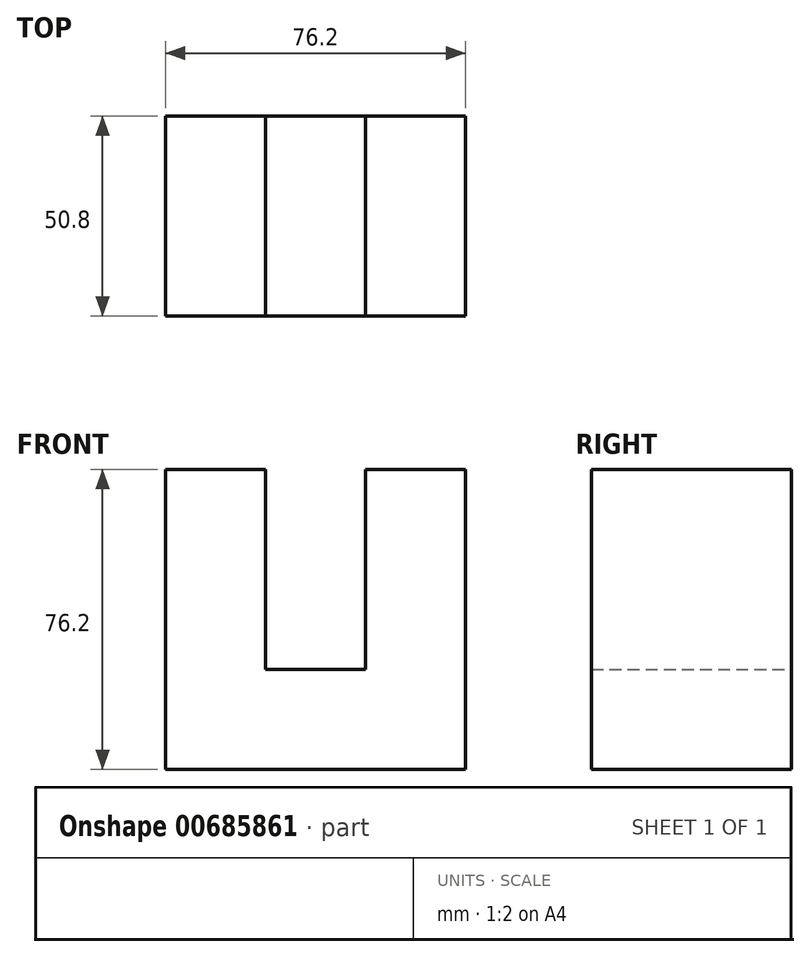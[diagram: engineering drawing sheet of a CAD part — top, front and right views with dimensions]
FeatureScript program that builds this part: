
annotation { "Feature Type Name" : "Feature", "Feature Type Description" : "" }
export const myFeature = defineFeature(function(context is Context, id is Id, definition is map)
    precondition{}
    {
        {
            var Q0;
            Q0=qCreatedBy(makeId("Front.planeOp"),FACE);
            var sketch = newSketch(context, id + "F0", { "sketchPlane" : qUnion([Q0])});
            skLineSegment(sketch, "E0", {"start": v(-27.97, 33.33) * mm, "end": v(-27.97, -42.87) * mm});
            skLineSegment(sketch, "E1", {"start": v(-27.97, 33.33) * mm, "end": v(-2.57, 33.33) * mm});
            skLineSegment(sketch, "E2", {"start": v(-2.57, 33.33) * mm, "end": v(-2.57, -17.47) * mm});
            skLineSegment(sketch, "E3", {"start": v(-2.57, -17.47) * mm, "end": v(22.83, -17.47) * mm});
            skLineSegment(sketch, "E4", {"start": v(22.83, -17.47) * mm, "end": v(22.83, 33.33) * mm});
            skLineSegment(sketch, "E5", {"start": v(22.83, 33.33) * mm, "end": v(48.23, 33.33) * mm});
            skLineSegment(sketch, "E6", {"start": v(48.23, 33.33) * mm, "end": v(48.23, -42.87) * mm});
            skLineSegment(sketch, "E7", {"start": v(48.23, -42.87) * mm, "end": v(-27.97, -42.87) * mm});
            skSolve(sketch);
        }
        {
            var Q0;
            Q0 = qSketchRegion(id + "F0", true);
            extrude(context, id + "F1", {"entities" : qUnion([Q0]), "depth" : 50.8 * mm, "offsetDistance" : 25.4 * mm});
        }
    });
